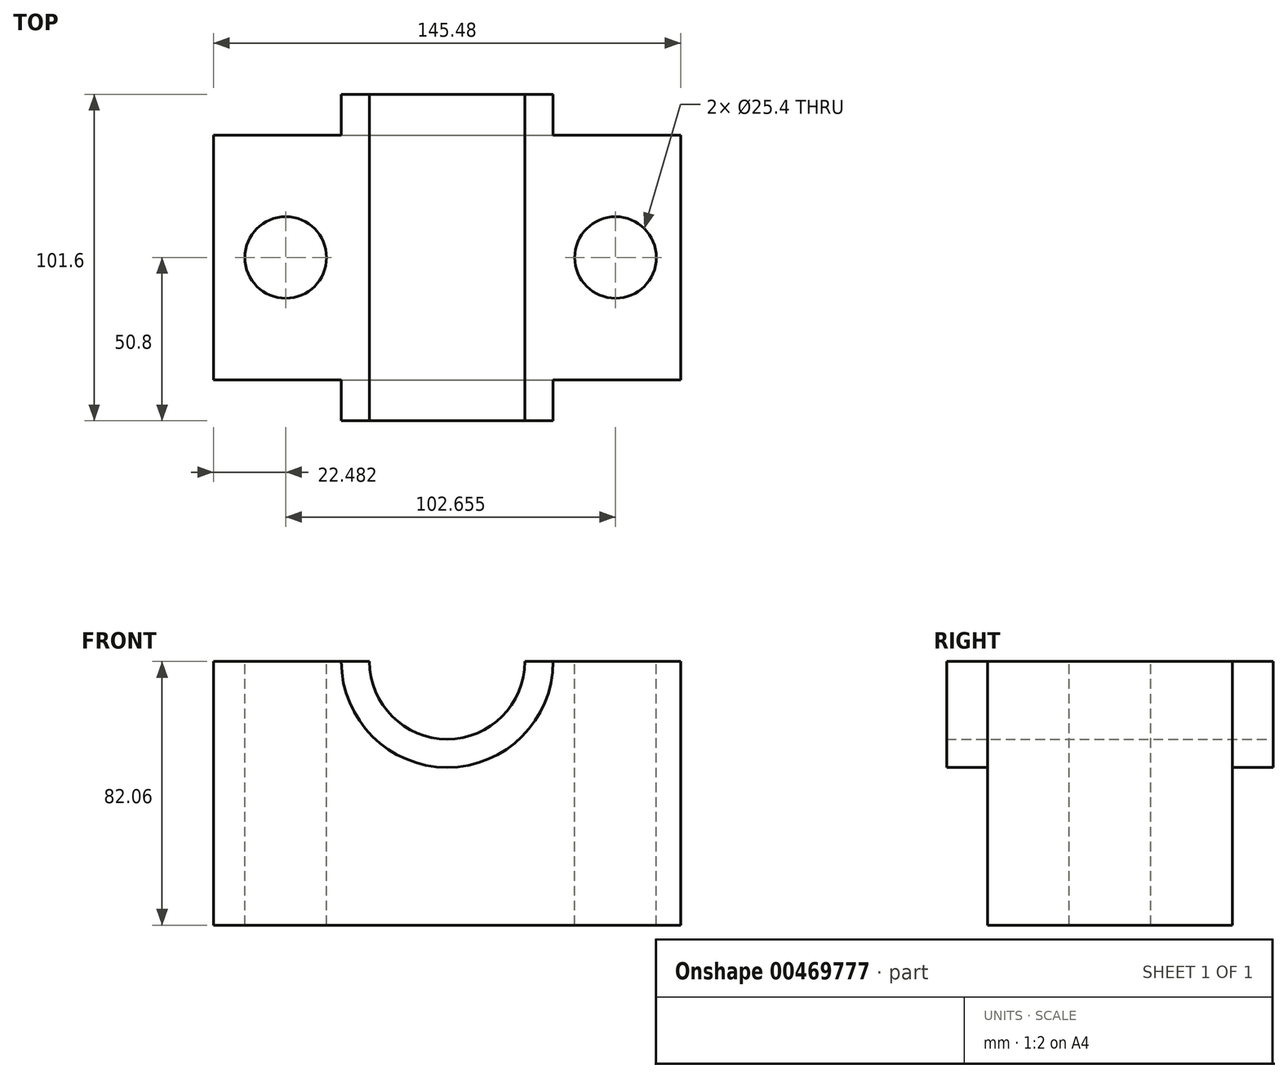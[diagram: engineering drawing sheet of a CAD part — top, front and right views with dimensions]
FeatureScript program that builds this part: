
annotation { "Feature Type Name" : "Feature", "Feature Type Description" : "" }
export const myFeature = defineFeature(function(context is Context, id is Id, definition is map)
    precondition{}
    {
        {
            var Q0;
            Q0=qCreatedBy(makeId("Front.planeOp"),FACE);
            var sketch = newSketch(context, id + "F0", { "sketchPlane" : qUnion([Q0])});
            skLineSegment(sketch, "E0.bottom", {"start": v(-72.74, 41.03) * mm, "end": v(72.74, 41.03) * mm});
            skLineSegment(sketch, "E0.top", {"start": v(-72.74, -41.03) * mm, "end": v(72.74, -41.03) * mm});
            skLineSegment(sketch, "E0.left", {"start": v(-72.74, 41.03) * mm, "end": v(-72.74, -41.03) * mm});
            skLineSegment(sketch, "E0.right", {"start": v(72.74, 41.03) * mm, "end": v(72.74, -41.03) * mm});
            skPoint(sketch, "E0.middle", {"position": v(0, 0) * mm});
            skSolve(sketch);
        }
        {
            var Q0;
            Q0=makeQuery(id+"F0.imprint","IMPRINT",FACE,{"disambiguationData":[TD([[makeQuery(id+"F0.imprint","IMPRINT",EDGE,{"derivedFrom":sQuery(id+"F0.wireOp",EDGE,"E0.bottom")}),-1.0]])]});
            extrude(context, id + "F1", {"entities" : qUnion([Q0]), "endBound" : BoundingType.SYMMETRIC, "depth" : 76.2 * mm});
        }
        {
            var Q0;
            Q0=makeQuery(id+"F1.opExtrude","CAP_FACE",FACE,{"disambiguationData":[OSD([sQuery(id+"F0.wireOp",EDGE,"E0.bottom"),sQuery(id+"F0.wireOp",EDGE,"E0.top"),sQuery(id+"F0.wireOp",EDGE,"E0.left"),sQuery(id+"F0.wireOp",EDGE,"E0.right")])],"isStart":false});
            var sketch = newSketch(context, id + "F2", { "sketchPlane" : qUnion([Q0])});
            skArc(sketch, "E1", {"start": v(-32.96, 41.03) * mm, "mid": v(0, 8.08) * mm, "end": v(32.96, 41.03) * mm});
            skArc(sketch, "E2", {"start": v(-24.17, 41.03) * mm, "mid": v(0, 16.87) * mm, "end": v(24.17, 41.03) * mm});
            skLineSegment(sketch, "E3", {"start": v(-32.96, 41.03) * mm, "end": v(-24.17, 41.03) * mm});
            skLineSegment(sketch, "E4", {"start": v(-24.17, 41.03) * mm, "end": v(-32.96, 41.03) * mm});
            skLineSegment(sketch, "E5", {"start": v(24.17, 41.03) * mm, "end": v(32.96, 41.03) * mm});
            skLineSegment(sketch, "E6", {"start": v(32.96, 41.03) * mm, "end": v(24.17, 41.03) * mm});
            skSolve(sketch);
        }
        {
            var Q0;
            Q0=makeQuery(id+"F2.imprint","IMPRINT",FACE,{"disambiguationData":[TD([[makeQuery(id+"F2.imprint","IMPRINT",EDGE,{"derivedFrom":sQuery(id+"F2.wireOp",EDGE,"E1")}),1.0]])]});
            extrude(context, id + "F3", {"entities" : qUnion([Q0]), "operationType" : NewBodyOperationType.ADD, "depth" : 12.7 * mm, "hasSecondDirection" : true, "secondDirectionOppositeDirection" : true, "secondDirectionDepth" : 88.9 * mm});
        }
        {
            var Q0;
            {var subQ0=sQuery(id+"F0.wireOp",EDGE,"E0.bottom");Q0=makeQuery(id+"F3.boolean.opBoolean","SPLIT",FACE,{"disambiguationData":[TD([makeQuery(id+"F3.opExtrude","SWEPT_FACE",FACE,{"disambiguationData":[OSD([sQuery(id+"F2.wireOp",EDGE,"E2")])]})])],"derivedFrom":makeQuery(id+"F1.opExtrude","CAP_FACE",FACE,{"disambiguationData":[OSD([subQ0,sQuery(id+"F0.wireOp",EDGE,"E0.top"),sQuery(id+"F0.wireOp",EDGE,"E0.left"),sQuery(id+"F0.wireOp",EDGE,"E0.right")])],"isStart":false})});}
            extrude(context, id + "F4", {"entities" : qUnion([Q0]), "operationType" : NewBodyOperationType.REMOVE, "endBound" : BoundingType.THROUGH_ALL, "oppositeDirection" : true, "depth" : 25.4 * mm});
        }
        {
            var Q0;
            {var subQ2=sQuery(id+"F0.wireOp",EDGE,"E0.left");var subQ4=sQuery(id+"F0.wireOp",EDGE,"E0.bottom");var subQ6=sQuery(id+"F2.wireOp",EDGE,"E6");var subQ7=sQuery(id+"F2.wireOp",EDGE,"E4");Q0=makeQuery(id+"F4.boolean.opBoolean","SPLIT",FACE,{"disambiguationData":[TD([makeQuery(id+"F1.opExtrude","SWEPT_FACE",FACE,{"disambiguationData":[OSD([subQ2])]})])],"derivedFrom":makeQuery(id+"F3.boolean.opBoolean","MERGE",FACE,{"derivedFrom":[makeQuery(id+"F1.opExtrude","SWEPT_FACE",FACE,{"disambiguationData":[OSD([subQ4])]}),makeQuery(id+"F3.opExtrude","SWEPT_FACE",FACE,{"disambiguationData":[OSD([subQ7])]}),makeQuery(id+"F3.opExtrude","SWEPT_FACE",FACE,{"disambiguationData":[OSD([subQ6])]})]})});}
            var sketch = newSketch(context, id + "F5", { "sketchPlane" : qUnion([Q0])});
            skPoint(sketch, "E7", {"position": v(-50.26, 0) * mm});
            skPoint(sketch, "E8", {"position": v(52.4, 0) * mm});
            skSolve(sketch);
        }
        {
            var Q0;
            Q0=sQuery(id+"F5.wireOp",VERTEX,"E7");
            var Q1;
            Q1=sQuery(id+"F5.wireOp",VERTEX,"E8");
            var Q2;
            Q2=makeQuery(id+"F1.opExtrude","SWEPT_BODY",BODY,{"disambiguationData":[OSD([sQuery(id+"F0.wireOp",EDGE,"E0.bottom"),sQuery(id+"F0.wireOp",EDGE,"E0.top"),sQuery(id+"F0.wireOp",EDGE,"E0.left"),sQuery(id+"F0.wireOp",EDGE,"E0.right")])]});
            hole(context, id + "F6", {"style" : HoleStyle.SIMPLE, "endStyle" : HoleEndStyle.THROUGH, "holeDiameter" : 25.4 * mm, "isTappedThrough" : true, "tappedDepth" : 12.7 * mm, "tapClearance" : 3, "locations" : qUnion([Q0, Q1]), "scope" : qUnion([Q2])});
        }
    });
